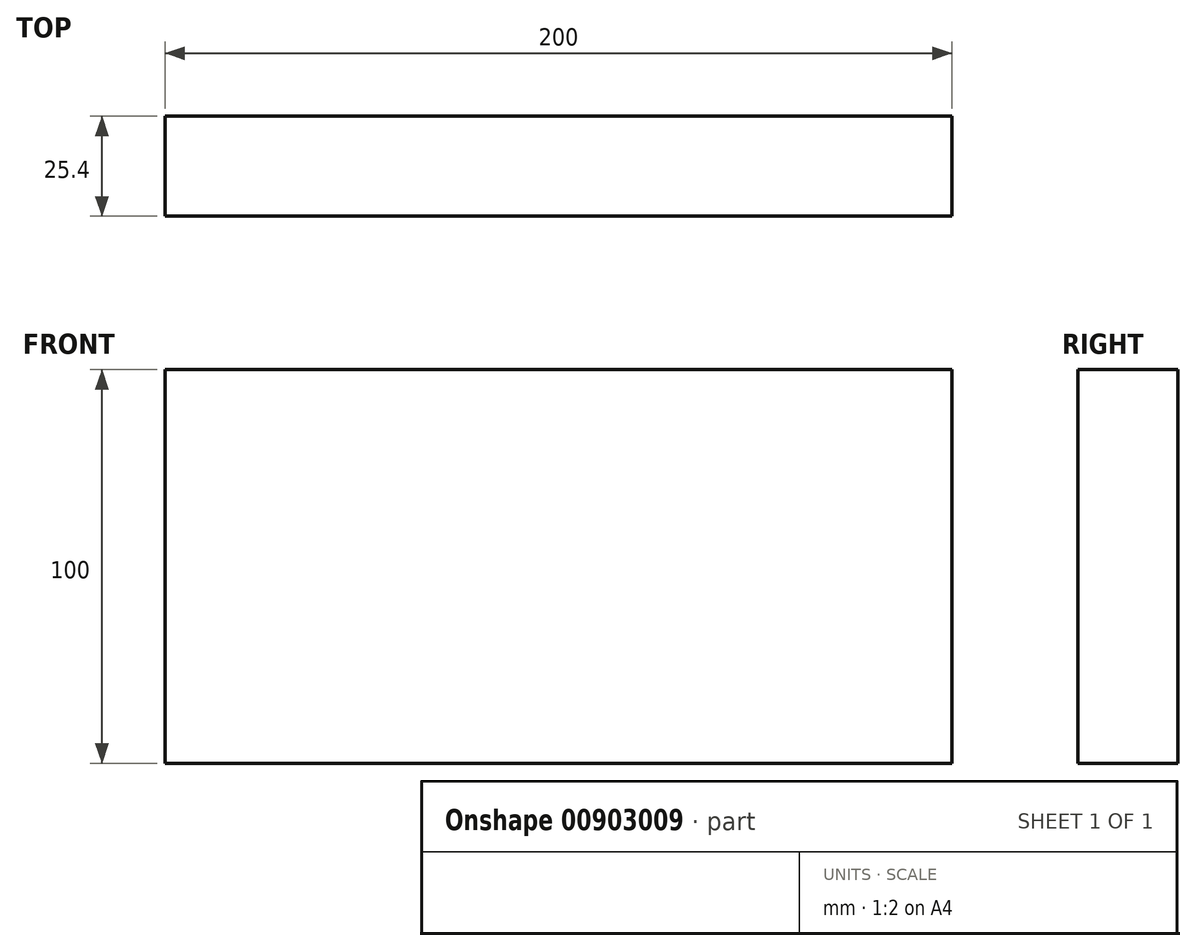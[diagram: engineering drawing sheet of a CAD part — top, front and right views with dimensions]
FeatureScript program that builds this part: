
annotation { "Feature Type Name" : "Feature", "Feature Type Description" : "" }
export const myFeature = defineFeature(function(context is Context, id is Id, definition is map)
    precondition{}
    {
        {
            var Q0;
            Q0=qCreatedBy(makeId("Front.planeOp"),FACE);
            var sketch = newSketch(context, id + "F0", { "sketchPlane" : qUnion([Q0])});
            skLineSegment(sketch, "E0.bottom", {"start": v(-100, 50) * mm, "end": v(100, 50) * mm});
            skLineSegment(sketch, "E0.top", {"start": v(-100, -50) * mm, "end": v(100, -50) * mm});
            skLineSegment(sketch, "E0.left", {"start": v(-100, 50) * mm, "end": v(-100, -50) * mm});
            skLineSegment(sketch, "E0.right", {"start": v(100, 50) * mm, "end": v(100, -50) * mm});
            skPoint(sketch, "E0.middle", {"position": v(0, 0) * mm});
            skSolve(sketch);
        }
        {
            var Q0;
            Q0=makeQuery(id+"F0.imprint","IMPRINT",FACE,{"disambiguationData":[TD([[makeQuery(id+"F0.imprint","IMPRINT",EDGE,{"derivedFrom":sQuery(id+"F0.wireOp",EDGE,"E0.bottom")}),-1.0]])]});
            extrude(context, id + "F1", {"entities" : qUnion([Q0]), "depth" : 25.4 * mm, "offsetDistance" : 25.4 * mm});
        }
    });
